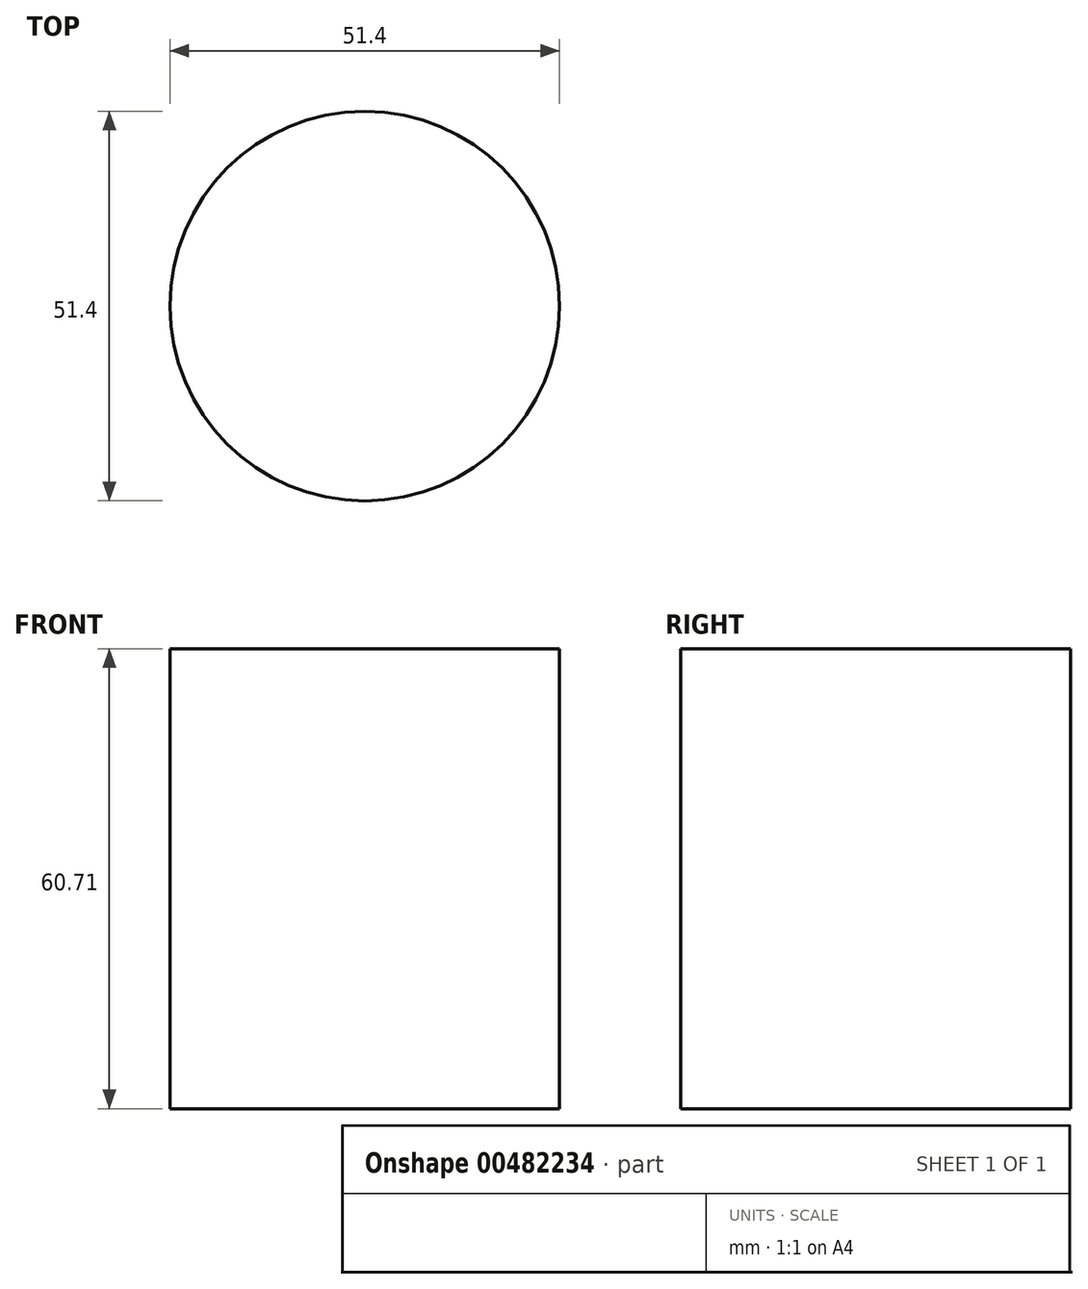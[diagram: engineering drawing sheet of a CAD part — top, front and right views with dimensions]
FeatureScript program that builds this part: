
annotation { "Feature Type Name" : "Feature", "Feature Type Description" : "" }
export const myFeature = defineFeature(function(context is Context, id is Id, definition is map)
    precondition{}
    {
        {
            var Q0;
            Q0=qCreatedBy(makeId("Top.planeOp"),FACE);
            var sketch = newSketch(context, id + "F0", { "sketchPlane" : qUnion([Q0])});
            skCircle(sketch, "E0", {"center": v(0, 0) * mm, "radius": 25.7 * mm});
            skSolve(sketch);
        }
        {
            var Q0;
            Q0=makeQuery(id+"F0.imprint","IMPRINT",FACE,{"disambiguationData":[TD([[makeQuery(id+"F0.imprint","IMPRINT",EDGE,{"derivedFrom":sQuery(id+"F0.wireOp",EDGE,"E0")}),1.0]])]});
            extrude(context, id + "F1", {"entities" : qUnion([Q0]), "depth" : 60.7 * mm});
        }
    });
